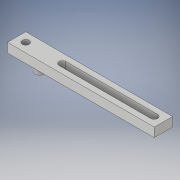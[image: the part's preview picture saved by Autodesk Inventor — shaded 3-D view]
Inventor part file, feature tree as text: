
AUTODESK INVENTOR PART (.ipt)
format: ipt  version: 2019 (Build 230136000, 136)  size: 122,880 bytes
history: native  units: in
note: dims shown in document units (in); Inventor stores cm internally (conversion verified against a paired STEP export)
features: sketch x3, extrude x2, hole x1
ambient origin geometry x8: Origin, YZ Plane, XZ Plane, XY Plane, X Axis, Y Axis, Z Axis, Center Point
bodies: Solid1 (feature_tree)
feature tree (6):
  extrude  "Extrusion1"  Depth=0.3937in
  hole  "Hole2"  [1 undecoded]
  extrude  "Extrusion2"  Depth=0.1969in
  sketch  "Sketch1"  dims[d0=3.1496in d1=0.3937in]
  sketch  "Sketch2"  dims[d2=0.1495in d3=0.1495in]
  sketch  "Sketch3"  dims[d4=0.9843in d5=0.1969in d6=0.1969in d7=0.0in d8=0.1969in d16=0.1969in d17=0.1495in d18=0.2362in d19=0.279in d20=0.0787in d21=0.5635in d22=0.315in d23=0.8108in d24=0.1969in d26=0.2953in d27=0.1969in d28=0.0in]
note: 1 required parameter value undecoded (feature->parameter linkage not recoverable at this tier; creation-order binding heuristic only, values carry confidence <= 0.55)
